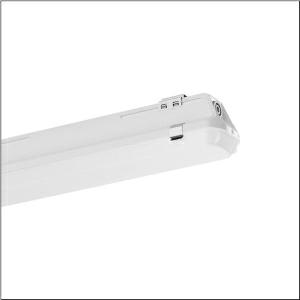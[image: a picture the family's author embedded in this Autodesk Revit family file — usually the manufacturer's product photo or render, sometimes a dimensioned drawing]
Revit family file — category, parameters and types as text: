
# Revit family: monsun_r__21_51fb10dp430b_6f0c
name_source: partatom
category: Lighting Fixtures
units: mm (PartAtom-declared; Revit-internal decimal feet)

## family parameters
Cut with Voids When Loaded = No
Host = Face
Light Source = No
Part Type = Normal
Room Calculation Point = No
Round Connector Dimension = Use Diameter
Shared = No

## types (1)
- --- (1 x LED, 3860 lm, 24.7 W, 4000K)
    Apparent Load = 25 VA
    CIE Flux Codes = 47 77 93 94 100
    Color Rendering = 80
    Color Temperature = 4000K
    Default Elevation = 1800 mm
    Description = Monsun® 21, damp-proof luminaire, chain hanger, primary optical cover: enclosure, of PMMA, light emission: direct distribution, primary light characteristic: symmetric, installation type: suspended mounting, surface-mounted, horizontal mounting, vertical mounting, LED, rated luminous flux: 3.860lm, luminous efficacy: 156lm/W, light colour: 840, colour temperature: 4000K, control gear: ECG DALI, with terminal, 5-pole, max. 2.5mm², mains connection: 220..240V, AC, 50/60Hz, rated input power: 25W, housing, of glass-fibre reinforced polyester, uncoated, bright grey, incl. chain hanger, length: 1.590mm, width: 90mm, height: 88mm, clip for enclosure, of stainless steel (V2A), ceiling mounting element, of stainless steel (V2A), chain hanger, of stainless steel (V2A), protection rating (complete): IP66, insulation class (complete): insulation class I (protective earthing), certification: CE, ENEC, VDE, UKCA, protection symbol: D, impact resistance: IK04, permissible operating ambient temperature: -25..+35°C, standard: EN 50419, EN 60598-2-1, corresponds to IFS (International Featured Standards) requirements for safety and quality in the food industry, for indoor or canopied outdoor use, no direct snow, no direct sun, no direct rain, contact your sales advisor before using the luminaires in applications with unclear chemical exposure, large temperature fluctuations or condensation-forming humidity, LABS conformity tested according to VDMA 24364:2018-05, packaging unit: 1 piece
    Height = 89 mm
    Lamp = 1 x LED
    Lamp Light Flux = 3860 lm
    Lamp Power = 24.7 W
    Lamp count = 1
    Length = 1590 mm
    Luminous efficacy = 156 lm/W
    Manufacturer = Siteco
    ModVariant = No
    Model = 51FB10DP430B
    Mounting Place = Ceiling
    Mounting Type = Surface mounted
    Number of Poles = 1
    OnlyDefault = Yes
    Power Factor = 1
    Product Name = Monsun® 21
    Product group = damp-proof luminaire
    ProductGroupID = 300
    Protection Class = Protection class I
    Protection Degree = IP 66
    RLX_Detail_Level = 1
    RLX_Emergency_Light_Flux = 0 lm
    RLX_Emergency_Type = 0
    RLX_Emergency_Type_DB = No
    RlxData = <blob elided: 92265 chars, md5=a9454453>
    Socket = socket
    Standby Power = 0 W
    System Light Flux = 3860 lm
    System Power = 25 W
    Type Comments = factory setting: luminous flux: 100 % | dim-lin: 254 | 162 mA
    Type Image = l_1319656.jpg
    URL = http://relux.com
    VarID = @adj_171347
    Voltage = 0 V
    Weight = 0.00 kg
    Width = 90 mm

## geometry (parser evidence)
native form markers: Blend x4, Sweep x14
no freeform markers — native parametric forms only
